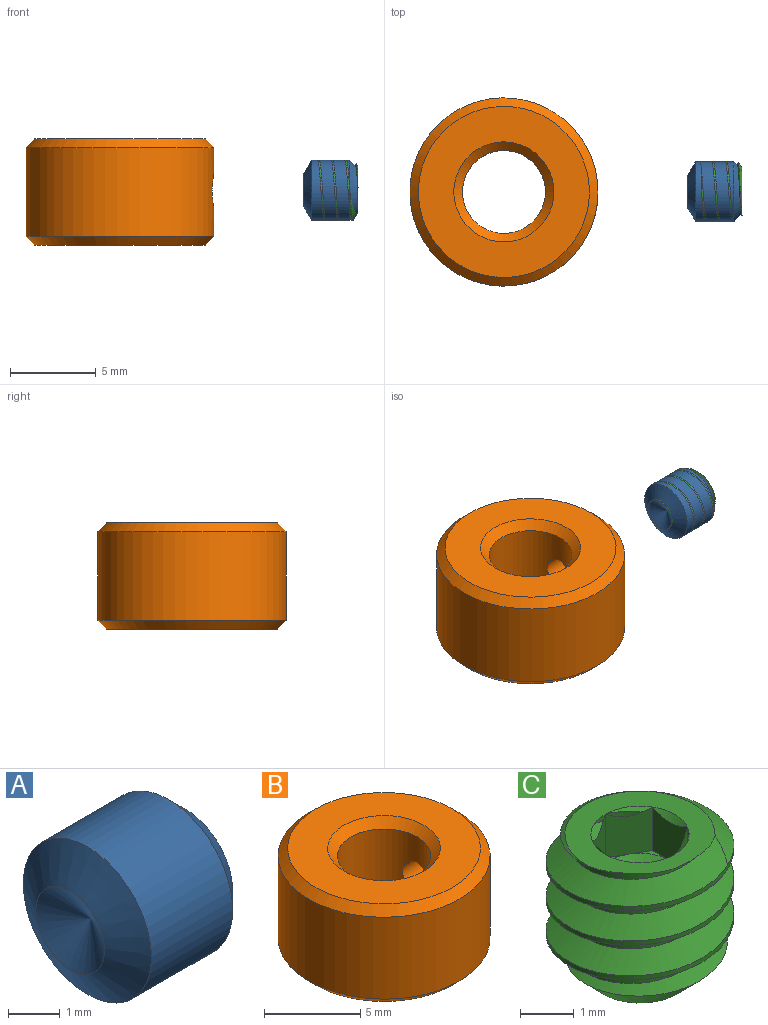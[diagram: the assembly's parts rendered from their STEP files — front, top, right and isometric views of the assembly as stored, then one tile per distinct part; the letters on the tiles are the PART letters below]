
ASSEMBLY  parts=3 mates=3
PART A: 12 faces, bbox 3.2x3.5x3.5 mm
  f0: cone r=1664.28mm half-angle=59deg, axis (-1,0,0), area 3.2mm2, adj f1
  f1: cone r=1.75mm half-angle=60deg, axis (1,0,0), area 7.9mm2, adj f0,f2
  f2: cylinder r=1.75mm len=3.51mm, axis (1,0,0), area 24.6mm2, adj f1,f3
  f3: cone r=1.28mm half-angle=45deg, axis (-1,0,0), area 6.4mm2, adj f2,f4
  f4: plane 2.56x2.56mm, normal (1,0,0), area 3mm2, adj f3,f5,f6,f7,f8,f9,f10
  f5: plane 2.03x0.86mm, normal (0,0.36,-0.93), area 1.9mm2, adj f4,f6,f10,f11
  f6: plane 2.03x0.72mm, normal (0,-0.63,-0.78), area 1.9mm2, adj f4,f5,f7,f11
  f7: plane 2.03x0.91mm, normal (0,-0.99,0.16), area 1.9mm2, adj f4,f6,f8,f11
  f8: plane 2.03x0.86mm, normal (0,-0.36,0.93), area 1.9mm2, adj f4,f7,f9,f11
  f9: plane 2.03x0.72mm, normal (0,0.63,0.78), area 1.9mm2, adj f4,f8,f10,f11
  f10: plane 2.03x0.91mm, normal (0,0.99,-0.16), area 1.9mm2, adj f4,f5,f9,f11
  f11: plane 1.81x1.71mm, normal (1,0,0), area 2.2mm2, adj f5,f6,f7,f8,f9,f10
PART B: 10 faces, bbox 11x11x6.2 mm
  f0: bspline ~2.16x2.1mm, area 1.4mm2, adj f1,f7
  f1: cylinder r=0.89mm len=3.11mm, axis (1,0,0), area 16.6mm2, adj f0,f6
  f2: cone r=2.93mm half-angle=45deg, axis (0,0,-1), area 11.9mm2, adj f6,f8
  f3: cone r=5.5mm half-angle=45deg, axis (0,0,1), area 23.3mm2, adj f7,f8
  f4: cone r=2.43mm half-angle=45deg, axis (0,0,1), area 11.9mm2, adj f6,f9
  f5: cone r=5mm half-angle=45deg, axis (0,0,-1), area 23.3mm2, adj f7,f9
  f6: cylinder r=2.43mm len=5.2mm, axis (0,0,1), area 77.6mm2, adj f1,f2,f4
  f7: cylinder r=5.5mm len=11mm, axis (0,0,1), area 176.1mm2, adj f0,f3,f5
  f8: plane 10x10mm, normal (0,0,-1), area 51.7mm2, adj f2,f3
  f9: plane 10x10mm, normal (0,0,1), area 51.7mm2, adj f4,f5
PART C: 27 faces, bbox 3.9x3.9x3.8 mm
  f0: cone r=0.79mm half-angle=60deg, axis (0,0,1), area 2.3mm2, adj f1,f22,f23,f24,f25,f26
  f1: plane 0.69x0.4mm, normal (0,0,1), area 0mm2, adj f0,f2,f21
  f2: plane 1.08x1.01mm, normal (-1,0,0), area 0.8mm2, adj f1,f3,f20,f21,f22
  f3: plane 1.34x1.14mm, normal (-0.5,-0.87,0), area 0.8mm2, adj f2,f4,f19,f22,f23
  f4: plane 1.34x1.14mm, normal (0.5,-0.87,0), area 0.8mm2, adj f3,f5,f18,f23,f24
  f5: plane 1.34x1.26mm, normal (1,0,0), area 0.8mm2, adj f4,f6,f17,f24,f25
  f6: plane 1.34x1.14mm, normal (0.5,0.87,0), area 0.8mm2, adj f5,f7,f21,f25,f26
  f7: cone r=0.92mm half-angle=45deg, axis (0,0,1), area 0mm2, adj f6,f8
  f8: plane 2.82x2.69mm, normal (0,0,1), area 3.2mm2, adj f7,f9,f10,f14,f15,f16,f17,f18
  f9: cone r=0.92mm half-angle=45deg, axis (0,0,1), area 0mm2, adj f8,f21
  f10: cylinder r=1.27mm len=2.86mm, axis (0,0,1), area 4mm2, adj f8,f11,f14,f16
  f11: cone r=0.96mm half-angle=45deg, axis (0,0,1), area 6mm2, adj f10,f12,f13,f14,f16
  f12: cylinder r=1.75mm len=3.51mm, axis (0,0,1), area 2.9mm2, adj f11,f14,f15,f16
  f13: cone r=1664.28mm half-angle=59deg, axis (0,0,-1), area 3.4mm2, adj f11
  f14: bspline ~3.5x3.5mm, area 16.8mm2, adj f8,f10,f11,f12,f15
  f15: cone r=1.75mm half-angle=55deg, axis (0,0,-1), area 1.6mm2, adj f8,f12,f14,f16
  f16: bspline ~3.5x3.5mm, area 16.8mm2, adj f8,f10,f11,f12,f15
  f17: cone r=0.92mm half-angle=45deg, axis (0,0,1), area 0mm2, adj f5,f8
  f18: cone r=0.92mm half-angle=45deg, axis (0,0,1), area 0mm2, adj f4,f8
  f19: cone r=0.92mm half-angle=45deg, axis (0,0,1), area 0mm2, adj f3,f8
  f20: cone r=0.92mm half-angle=45deg, axis (0,0,1), area 0.1mm2, adj f2,f8
  f21: plane 1.34x1.14mm, normal (-0.5,0.87,0), area 0.8mm2, adj f1,f2,f6,f9,f26
  f22: plane 0.69x0.4mm, normal (0,0,1), area 0mm2, adj f0,f2,f3
  f23: plane 0.79x0.23mm, normal (0,0,1), area 0mm2, adj f0,f3,f4
  f24: plane 0.69x0.4mm, normal (0,0,1), area 0mm2, adj f0,f4,f5
  f25: plane 0.69x0.4mm, normal (0,0,1), area 0mm2, adj f0,f5,f6
  f26: plane 0.79x0.23mm, normal (0,0,1), area 0mm2, adj f0,f6,f21
PLACE A rot(axis=(-1,0,0),7.9deg) t=(7.76,0.03,0.05)mm
PLACE B at identity fixed
PLACE C rot(axis=(0.55,0.63,0.55),115.6deg) t=(12.43,0.42,-0.1)mm
MATE planar C.f8 <-> A.f0  axis (1,0,0) through (13.73,0.48,-0.01)mm
MATE cylindrical C.f0 <-> B.f1  axis (1,0,0) through (10.55,0.42,-0.1)mm
MATE cylindrical A.f1 <-> C.f13  axis (1,0,0) through (10.55,0.42,-0.1)mm
